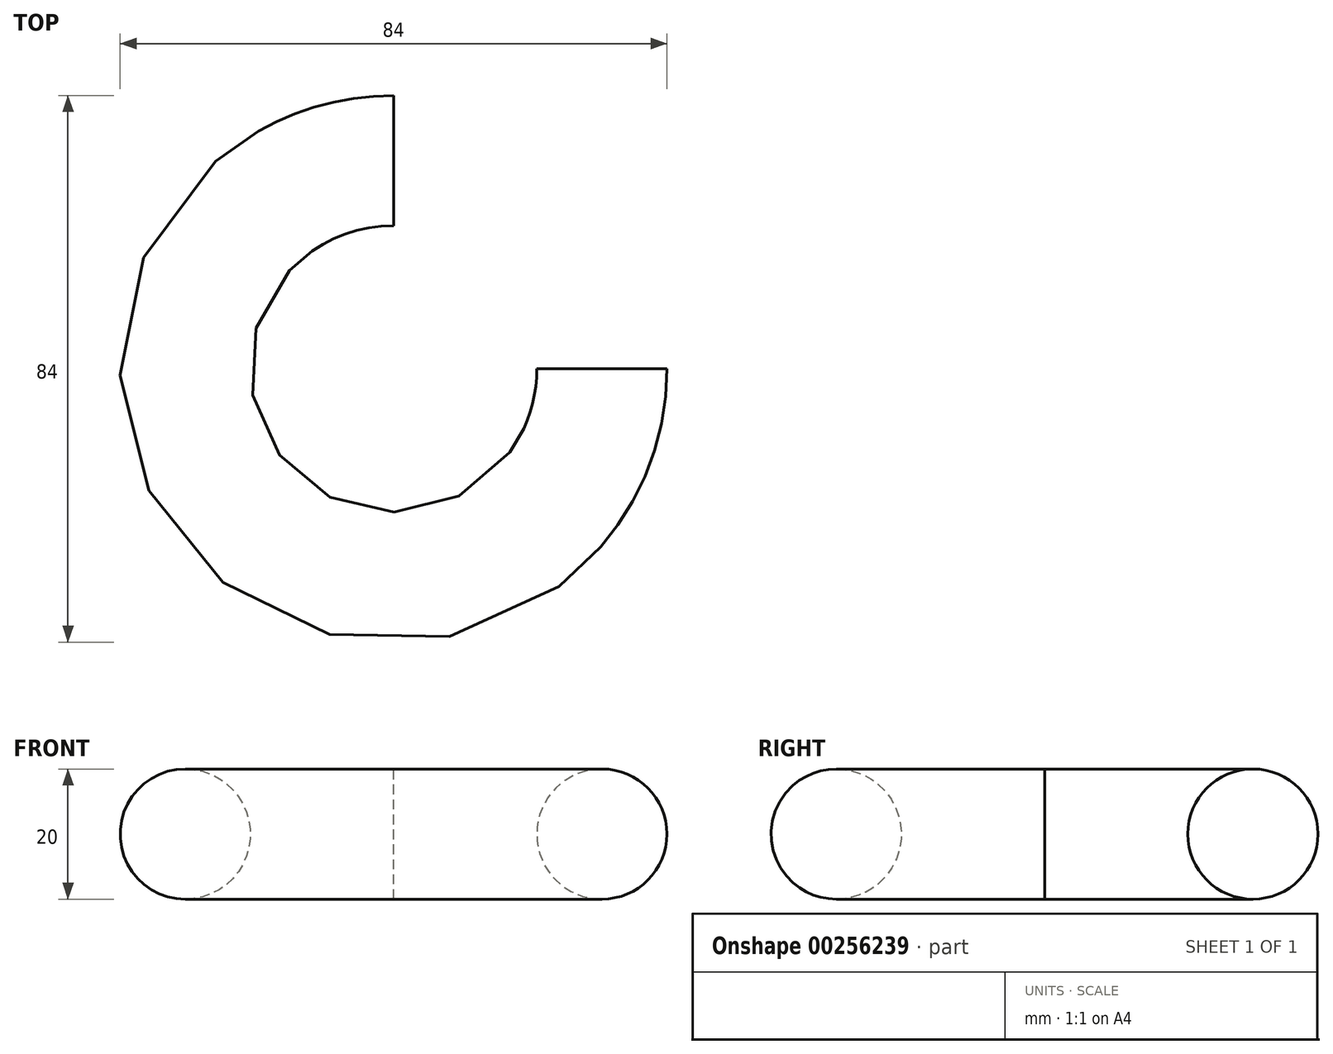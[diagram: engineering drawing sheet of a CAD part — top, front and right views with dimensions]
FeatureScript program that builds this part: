
annotation { "Feature Type Name" : "Feature", "Feature Type Description" : "" }
export const myFeature = defineFeature(function(context is Context, id is Id, definition is map)
    precondition{}
    {
        {
            var Q0;
            Q0=qCreatedBy(makeId("Front.planeOp"),FACE);
            var sketch = newSketch(context, id + "F0", { "sketchPlane" : qUnion([Q0])});
            skCircle(sketch, "E0", {"center": v(32, 0) * mm, "radius": 10 * mm});
            skLineSegment(sketch, "E1", {"start": v(0, 40.6) * mm, "end": v(0, -50.95) * mm, "construction": true});
            skSolve(sketch);
        }
        {
            var Q0;
            Q0=makeQuery(id+"F0.imprint","IMPRINT",FACE,{"disambiguationData":[TD([[makeQuery(id+"F0.imprint","IMPRINT",EDGE,{"derivedFrom":sQuery(id+"F0.wireOp",EDGE,"E0")}),1.0]])]});
            var Q1;
            Q1=sQuery(id+"F0.wireOp",EDGE,"E1");
            var Q2;
            Q2=sQuery(id+"F0.wireOp",EDGE,"E1");
            revolve(context, id + "F1", {"entities" : qUnion([Q0]), "surfaceEntities" : qUnion([Q1]), "axis" : qUnion([Q2]), "revolveType" : RevolveType.ONE_DIRECTION, "angle" : 270 * degree});
        }
    });
